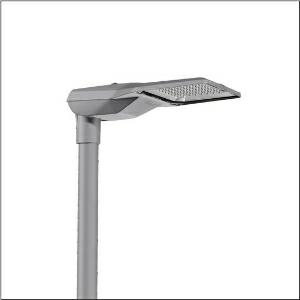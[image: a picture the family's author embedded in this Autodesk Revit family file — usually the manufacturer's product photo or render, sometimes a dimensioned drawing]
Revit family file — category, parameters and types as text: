
# Revit family: streetlight_sl_21_midi___st1_5a_5xe3p43s08mb_00aa
name_source: partatom
category: Lighting Fixtures
units: mm (PartAtom-declared; Revit-internal decimal feet)

## family parameters
Cut with Voids When Loaded = No
Host = Face
Light Source = No
Part Type = Normal
Room Calculation Point = No
Round Connector Dimension = Use Diameter
Shared = No

## types (1)
- --- (1 x LED, 19830 lm, 147 W, 4000K)
    Apparent Load = 147 VA
    CIE Flux Codes = 22 53 95 100 100
    Color Rendering = 70
    Color Temperature = 4000K
    Default Elevation = 1800 mm
    Description = Streetlight SL 21 midi, mast luminaire, primary light control with lens, of PMMA, primary optical cover: cover, of toughened safety glass, transparent, light distribution: ST1.5a, light emission: direct distribution, primary light characteristic: asymmetric, installation type: side-entry, post-top, LED, High Power LED, rated luminous flux: 19.830lm, luminous efficacy: 135lm/W, light colour: 740, colour temperature: 4000K, control gear: D4i, control: overheat protection, constant luminous flux control, time-dependent luminous flux control, flexible luminous flux parameterisation, pre-setting: logarithmic dimming characteristic, mains connection: 230..240V, AC, 50/60Hz, start of lifetime: 147W, end of service life: 155W, reduction: 65W, luminaire housing, of diecast aluminium, powder-coated, Siteco® metallic grey (DB 702S), corrosivity category C5 mid according to DIN EN ISO 12944, please order mast flange separately, inclination adjustable: 0°, 5°, 10°, 15°, sealing non-destructively replaceable, multi-level sealing system, length: 644mm, width: 335mm, height: 110mm, mast flange for spigot size: 42mm (side-entry): 5XC10008XM4, 60/48mm (side-entry/post-top): 5XC10108XM2, 76/60mm (side-entry/post-top): 5XC10108XM1, mounting height: 4..8m, Smart Interface above, protection rating (complete): IP66, insulation class (complete): insulation class II (safety insulation), certification: CE, ENEC, ENEC+, VDE, impact resistance: IK10, permissible operating ambient temperature for outdoor applications: -40..+50°C, standard-compliant lighting for roads and squares, packaging unit: 1 piece

Light Distribution: ST1.5a
    Height = 111 mm
    Lamp = 1 x LED
    Lamp Light Flux = 19830 lm
    Lamp Power = 147 W
    Lamp count = 1
    Length = 644 mm
    Luminous efficacy = 135 lm/W
    Manufacturer = Siteco
    ModVariant = No
    Model = 5XE3P43S08MB
    Number of Poles = 1
    OnlyDefault = Yes
    Power Factor = 1
    Product Name = Streetlight SL 21 midi | ST1.5a
    Product group = mast luminaire | pylon top
    ProductGroupID = 6100
    Protection Class = Protection class II
    Protection Degree = IP 66
    RLX_Detail_Level = 1
    RLX_Emergency_Light_Flux = 0 lm
    RLX_Emergency_Type = 0
    RLX_Emergency_Type_DB = No
    RlxData = <blob elided: 30357 chars, md5=600965b4>
    Socket = socket
    Standby Power = 0 W
    System Light Flux = 19830 lm
    System Power = 147 W
    Type Comments = factory setting: luminous flux: 100 % | dim-lin: 254 | 750 mA
    Type Image = l_1004302.jpg
    URL = http://relux.com
    VarID = @adj_197609
    Voltage = 0 V
    Weight = 0.00 kg
    Width = 336 mm

## geometry (parser evidence)
native form markers: Blend x4, Sweep x9
no freeform markers — native parametric forms only
